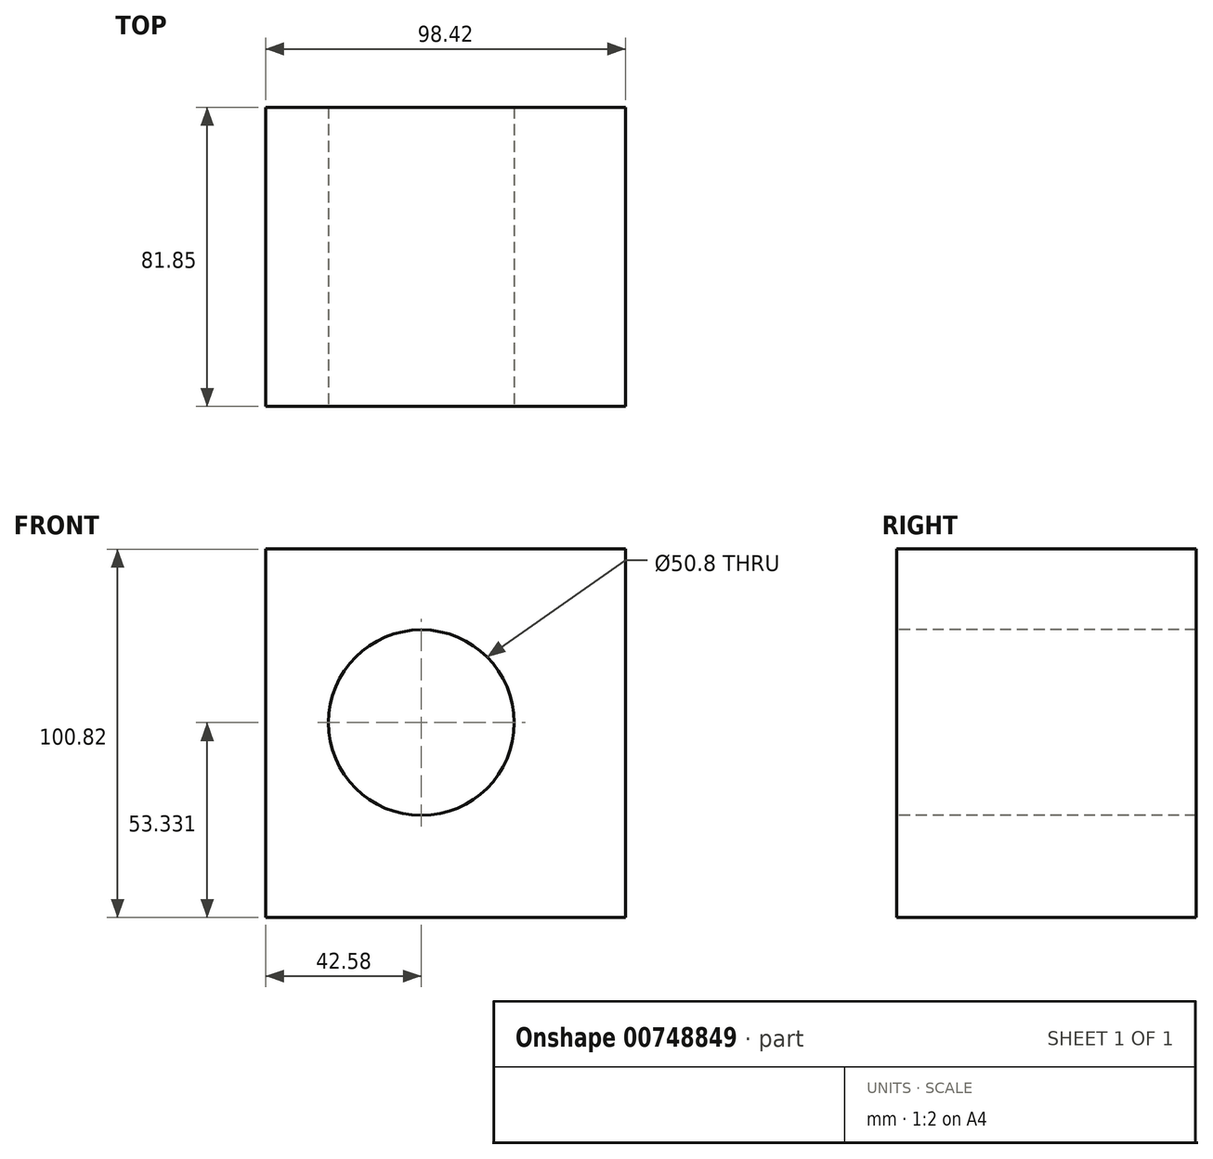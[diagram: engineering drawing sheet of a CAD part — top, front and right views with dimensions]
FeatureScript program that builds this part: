
annotation { "Feature Type Name" : "Feature", "Feature Type Description" : "" }
export const myFeature = defineFeature(function(context is Context, id is Id, definition is map)
    precondition{}
    {
        {
            var Q0;
            Q0=qCreatedBy(makeId("Front.planeOp"),FACE);
            var sketch = newSketch(context, id + "F0", { "sketchPlane" : qUnion([Q0])});
            skLineSegment(sketch, "E0.bottom", {"start": v(-42.58, -33) * mm, "end": v(55.84, -33) * mm});
            skLineSegment(sketch, "E0.top", {"start": v(-42.58, 67.82) * mm, "end": v(55.84, 67.82) * mm});
            skLineSegment(sketch, "E0.left", {"start": v(-42.58, -33) * mm, "end": v(-42.58, 67.82) * mm});
            skLineSegment(sketch, "E0.right", {"start": v(55.84, -33) * mm, "end": v(55.84, 67.82) * mm});
            skSolve(sketch);
        }
        {
            var Q0;
            Q0 = qSketchRegion(id + "F0", true);
            extrude(context, id + "F1", {"entities" : qUnion([Q0]), "depth" : 81.85 * mm, "offsetDistance" : 25.4 * mm});
        }
        {
            var Q0;
            Q0=makeQuery(id+"F1.opExtrude","CAP_FACE",FACE,{"disambiguationData":[OSD([sQuery(id+"F0.wireOp",EDGE,"E0.bottom"),sQuery(id+"F0.wireOp",EDGE,"E0.top"),sQuery(id+"F0.wireOp",EDGE,"E0.left"),sQuery(id+"F0.wireOp",EDGE,"E0.right")])],"isStart":false});
            var sketch = newSketch(context, id + "F2", { "sketchPlane" : qUnion([Q0])});
            skPoint(sketch, "E1", {"position": v(0, 20.33) * mm});
            skSolve(sketch);
        }
        {
            var Q0;
            Q0=sQuery(id+"F2.wireOp",VERTEX,"E1");
            var Q1;
            Q1=makeQuery(id+"F1.opExtrude","SWEPT_BODY",BODY,{"disambiguationData":[OSD([sQuery(id+"F0.wireOp",EDGE,"E0.bottom"),sQuery(id+"F0.wireOp",EDGE,"E0.top"),sQuery(id+"F0.wireOp",EDGE,"E0.left"),sQuery(id+"F0.wireOp",EDGE,"E0.right")])]});
            hole(context, id + "F3", {"style" : HoleStyle.SIMPLE, "endStyle" : HoleEndStyle.THROUGH, "holeDiameter" : 50.8 * mm, "majorDiameter" : 6.35 * mm, "isTappedThrough" : true, "tappedDepth" : 12.7 * mm, "tapClearance" : 3, "locations" : qUnion([Q0]), "scope" : qUnion([Q1])});
        }
    });
